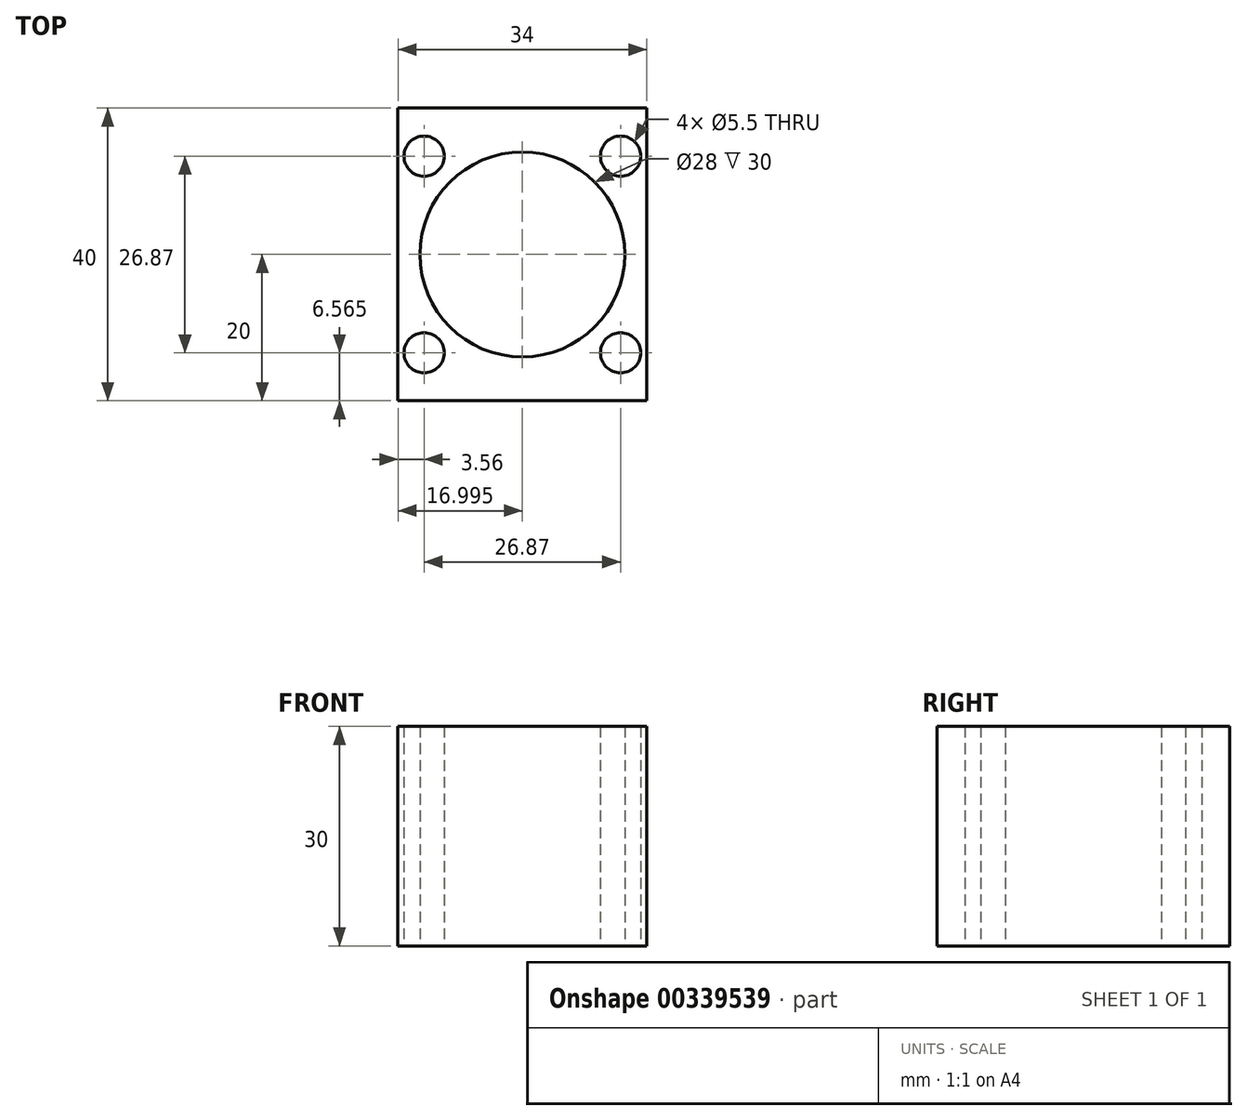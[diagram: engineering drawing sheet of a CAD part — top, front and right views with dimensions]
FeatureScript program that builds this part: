
annotation { "Feature Type Name" : "Feature", "Feature Type Description" : "" }
export const myFeature = defineFeature(function(context is Context, id is Id, definition is map)
    precondition{}
    {
        {
            var Q0;
            Q0=qCreatedBy(makeId("Top.planeOp"),FACE);
            var sketch = newSketch(context, id + "F0", { "sketchPlane" : qUnion([Q0])});
            skCircle(sketch, "E0", {"center": v(-21.1, -2.5) * mm, "radius": 24 * mm});
            skCircle(sketch, "E1", {"center": v(-21.1, -2.5) * mm, "radius": 14 * mm});
            skCircle(sketch, "E2", {"center": v(-21.1, -2.5) * mm, "radius": 19 * mm});
            skCircle(sketch, "E3", {"center": v(-34.54, -15.94) * mm, "radius": 2.75 * mm});
            skCircle(sketch, "E4", {"center": v(-21.1, -21.5) * mm, "radius": 2.75 * mm});
            skCircle(sketch, "E5", {"center": v(-7.67, -15.94) * mm, "radius": 2.75 * mm});
            skCircle(sketch, "E6", {"center": v(-21.1, 16.5) * mm, "radius": 2.75 * mm});
            skCircle(sketch, "E7", {"center": v(-7.67, 10.94) * mm, "radius": 2.75 * mm});
            skLineSegment(sketch, "E8", {"start": v(-21.1, -2.5) * mm, "end": v(-21.1, 38.82) * mm, "construction": true});
            skLineSegment(sketch, "E9", {"start": v(-21.1, -2.5) * mm, "end": v(-21.1, -36.07) * mm, "construction": true});
            skLineSegment(sketch, "E10", {"start": v(-21.1, -2.5) * mm, "end": v(-52.03, 28.43) * mm, "construction": true});
            skLineSegment(sketch, "E11", {"start": v(-21.1, -2.5) * mm, "end": v(11.53, 30.14) * mm, "construction": true});
            skLineSegment(sketch, "E12", {"start": v(-21.1, -2.5) * mm, "end": v(4.4, -28) * mm, "construction": true});
            skLineSegment(sketch, "E13", {"start": v(-21.1, -2.5) * mm, "end": v(-47.97, -29.37) * mm, "construction": true});
            skLineSegment(sketch, "E14", {"start": v(-21.1, -2.5) * mm, "end": v(-21.1, -26.49) * mm, "construction": true});
            skCircle(sketch, "E15", {"center": v(-34.54, 10.94) * mm, "radius": 2.75 * mm});
            skLineSegment(sketch, "E16", {"start": v(-1.1, 21.62) * mm, "end": v(-1.1, -39.23) * mm});
            skLineSegment(sketch, "E17", {"start": v(-41.1, 18.06) * mm, "end": v(-41.1, -27.04) * mm});
            skLineSegment(sketch, "E18.bottom", {"start": v(-38.1, 17.5) * mm, "end": v(-4.1, 17.5) * mm});
            skLineSegment(sketch, "E18.top", {"start": v(-38.1, -22.5) * mm, "end": v(-4.1, -22.5) * mm});
            skLineSegment(sketch, "E18.left", {"start": v(-38.1, 17.5) * mm, "end": v(-38.1, -22.5) * mm});
            skLineSegment(sketch, "E18.right", {"start": v(-4.1, 17.5) * mm, "end": v(-4.1, -22.5) * mm});
            skSolve(sketch);
        }
        {
            var Q0;
            {var subQ8=sQuery(id+"F0.wireOp",EDGE,"E18.bottom");var subQ10=sQuery(id+"F0.wireOp",EDGE,"E0");var subQ11=makeQuery(id+"F0.imprint","INTERSECT",VERTEX,{"disambiguationData":[OD(1.0)],"derivedFrom":[subQ10,subQ8]});Q0=makeQuery(id+"F0.imprint","IMPRINT",FACE,{"disambiguationData":[TD([[makeQuery(id+"F0.imprint","IMPRINT",EDGE,{"disambiguationData":[TD([[subQ11,-1.0]])],"derivedFrom":subQ10}),1.0]])]});}
            var Q1;
            Q1=makeQuery(id+"F0.imprint","IMPRINT",FACE,{"disambiguationData":[TD([[makeQuery(id+"F0.imprint","IMPRINT",EDGE,{"derivedFrom":sQuery(id+"F0.wireOp",EDGE,"E1")}),-1.0]])]});
            var Q2;
            {var subQ8=sQuery(id+"F0.wireOp",EDGE,"E18.right");var subQ10=sQuery(id+"F0.wireOp",EDGE,"E0");var subQ11=makeQuery(id+"F0.imprint","INTERSECT",VERTEX,{"disambiguationData":[OD(0.0)],"derivedFrom":[subQ10,subQ8]});Q2=makeQuery(id+"F0.imprint","IMPRINT",FACE,{"disambiguationData":[TD([[makeQuery(id+"F0.imprint","IMPRINT",EDGE,{"disambiguationData":[TD([[subQ11,-1.0]])],"derivedFrom":subQ10}),1.0]])]});}
            var Q3;
            {var subQ0=sQuery(id+"F0.wireOp",EDGE,"E6");var subQ1=sQuery(id+"F0.wireOp",EDGE,"E2");var subQ2=makeQuery(id+"F0.imprint","INTERSECT",VERTEX,{"disambiguationData":[OD(0.0)],"derivedFrom":[subQ1,subQ0]});Q3=makeQuery(id+"F0.imprint","IMPRINT",FACE,{"disambiguationData":[TD([[makeQuery(id+"F0.imprint","IMPRINT",EDGE,{"disambiguationData":[TD([[subQ2,-1.0]])],"derivedFrom":subQ1}),1.0]])]});}
            var Q4;
            {var subQ0=sQuery(id+"F0.wireOp",EDGE,"E6");var subQ1=sQuery(id+"F0.wireOp",EDGE,"E2");var subQ2=makeQuery(id+"F0.imprint","INTERSECT",VERTEX,{"disambiguationData":[OD(0.0)],"derivedFrom":[subQ1,subQ0]});Q4=makeQuery(id+"F0.imprint","IMPRINT",FACE,{"disambiguationData":[TD([[makeQuery(id+"F0.imprint","IMPRINT",EDGE,{"disambiguationData":[TD([[subQ2,-1.0]])],"derivedFrom":subQ1}),-1.0]])]});}
            var Q5;
            {var subQ0=sQuery(id+"F0.wireOp",EDGE,"E4");var subQ1=sQuery(id+"F0.wireOp",EDGE,"E2");var subQ2=makeQuery(id+"F0.imprint","INTERSECT",VERTEX,{"disambiguationData":[OD(0.0)],"derivedFrom":[subQ1,subQ0]});Q5=makeQuery(id+"F0.imprint","IMPRINT",FACE,{"disambiguationData":[TD([[makeQuery(id+"F0.imprint","IMPRINT",EDGE,{"disambiguationData":[TD([[subQ2,-1.0]])],"derivedFrom":subQ1}),1.0]])]});}
            var Q6;
            {var subQ4=sQuery(id+"F0.wireOp",EDGE,"E18.left");var subQ5=sQuery(id+"F0.wireOp",EDGE,"E0");var subQ6=makeQuery(id+"F0.imprint","INTERSECT",VERTEX,{"disambiguationData":[OD(1.0)],"derivedFrom":[subQ5,subQ4]});Q6=makeQuery(id+"F0.imprint","IMPRINT",FACE,{"disambiguationData":[TD([[makeQuery(id+"F0.imprint","IMPRINT",EDGE,{"disambiguationData":[TD([[subQ6,-1.0]])],"derivedFrom":subQ5}),1.0]])]});}
            var Q7;
            {var subQ8=sQuery(id+"F0.wireOp",EDGE,"E18.top");var subQ10=sQuery(id+"F0.wireOp",EDGE,"E0");var subQ11=makeQuery(id+"F0.imprint","INTERSECT",VERTEX,{"disambiguationData":[OD(1.0)],"derivedFrom":[subQ10,subQ8]});Q7=makeQuery(id+"F0.imprint","IMPRINT",FACE,{"disambiguationData":[TD([[makeQuery(id+"F0.imprint","IMPRINT",EDGE,{"disambiguationData":[TD([[subQ11,-1.0]])],"derivedFrom":subQ10}),1.0]])]});}
            var Q8;
            {var subQ0=sQuery(id+"F0.wireOp",EDGE,"E18.top");var subQ1=sQuery(id+"F0.wireOp",EDGE,"E0");var subQ2=makeQuery(id+"F0.imprint","INTERSECT",VERTEX,{"disambiguationData":[OD(1.0)],"derivedFrom":[subQ1,subQ0]});Q8=makeQuery(id+"F0.imprint","IMPRINT",FACE,{"disambiguationData":[TD([[makeQuery(id+"F0.imprint","IMPRINT",EDGE,{"disambiguationData":[TD([[subQ2,-1.0]])],"derivedFrom":subQ1}),-1.0]])]});}
            var Q9;
            {var subQ0=sQuery(id+"F0.wireOp",EDGE,"E18.left");var subQ1=sQuery(id+"F0.wireOp",EDGE,"E0");var subQ2=makeQuery(id+"F0.imprint","INTERSECT",VERTEX,{"disambiguationData":[OD(1.0)],"derivedFrom":[subQ1,subQ0]});Q9=makeQuery(id+"F0.imprint","IMPRINT",FACE,{"disambiguationData":[TD([[makeQuery(id+"F0.imprint","IMPRINT",EDGE,{"disambiguationData":[TD([[subQ2,-1.0]])],"derivedFrom":subQ1}),-1.0]])]});}
            var Q10;
            {var subQ0=sQuery(id+"F0.wireOp",EDGE,"E18.bottom");var subQ1=sQuery(id+"F0.wireOp",EDGE,"E0");var subQ2=makeQuery(id+"F0.imprint","INTERSECT",VERTEX,{"disambiguationData":[OD(1.0)],"derivedFrom":[subQ1,subQ0]});Q10=makeQuery(id+"F0.imprint","IMPRINT",FACE,{"disambiguationData":[TD([[makeQuery(id+"F0.imprint","IMPRINT",EDGE,{"disambiguationData":[TD([[subQ2,-1.0]])],"derivedFrom":subQ1}),-1.0]])]});}
            var Q11;
            {var subQ0=sQuery(id+"F0.wireOp",EDGE,"E18.right");var subQ1=sQuery(id+"F0.wireOp",EDGE,"E0");var subQ2=makeQuery(id+"F0.imprint","INTERSECT",VERTEX,{"disambiguationData":[OD(0.0)],"derivedFrom":[subQ1,subQ0]});Q11=makeQuery(id+"F0.imprint","IMPRINT",FACE,{"disambiguationData":[TD([[makeQuery(id+"F0.imprint","IMPRINT",EDGE,{"disambiguationData":[TD([[subQ2,-1.0]])],"derivedFrom":subQ1}),-1.0]])]});}
            var Q12;
            {var subQ0=sQuery(id+"F0.wireOp",EDGE,"E4");var subQ1=sQuery(id+"F0.wireOp",EDGE,"E2");var subQ2=makeQuery(id+"F0.imprint","INTERSECT",VERTEX,{"disambiguationData":[OD(0.0)],"derivedFrom":[subQ1,subQ0]});Q12=makeQuery(id+"F0.imprint","IMPRINT",FACE,{"disambiguationData":[TD([[makeQuery(id+"F0.imprint","IMPRINT",EDGE,{"disambiguationData":[TD([[subQ2,-1.0]])],"derivedFrom":subQ1}),-1.0]])]});}
            extrude(context, id + "F1", {"entities" : qUnion([Q0, Q1, Q2, Q3, Q4, Q5, Q6, Q7, Q8, Q9, Q10, Q11, Q12]), "depth" : 30 * mm, "offsetDistance" : 25 * mm});
        }
    });
